# Revit family: Storage-Mounted-Teknion-JNBSO-Open_Credenza_with_Lateral_File-R2015
name_source: partatom
category: Furniture
revit_build: Autodesk Revit Architecture 2015 (Build: 20140323_1530(x64)
units: mm (PartAtom-declared; Revit-internal decimal feet)

## types (2) — shared parameters
Assembly Code = E2020200
Description = Semi-Suspended Credenza – Open with Lateral File
Manufacturer = Teknion
Manufacturer Fax = 416.661.4586
Part Number = JNBSO
Product Documentation Link = http://www.teknion.com
Product Line = Expansion Cityline
Product Page URL = http://www.teknion.com
Series = Expansion Cityline
Sustainability Data = http://www.teknion.com
URL = www.teknion.com
Unit Weight URL = http://www.teknion.com
Warranty = http://www.teknion.com

## per-type parameters (varying)
| type | Depth of Cabinet Door | Front Finish | Has Metal Front Style | Has Solid Front Style | Model |
| Solid | 0.701 " | Source Laminate - Teknion - RV - Very White | No | Yes | JNBSOS |
| Metal | 0.118 " | Mica - Teknion - V - Satin - Very White | Yes | No | JNBSOM |

## geometry (parser evidence)
native form markers: Sweep x3
no freeform markers — native parametric forms only
